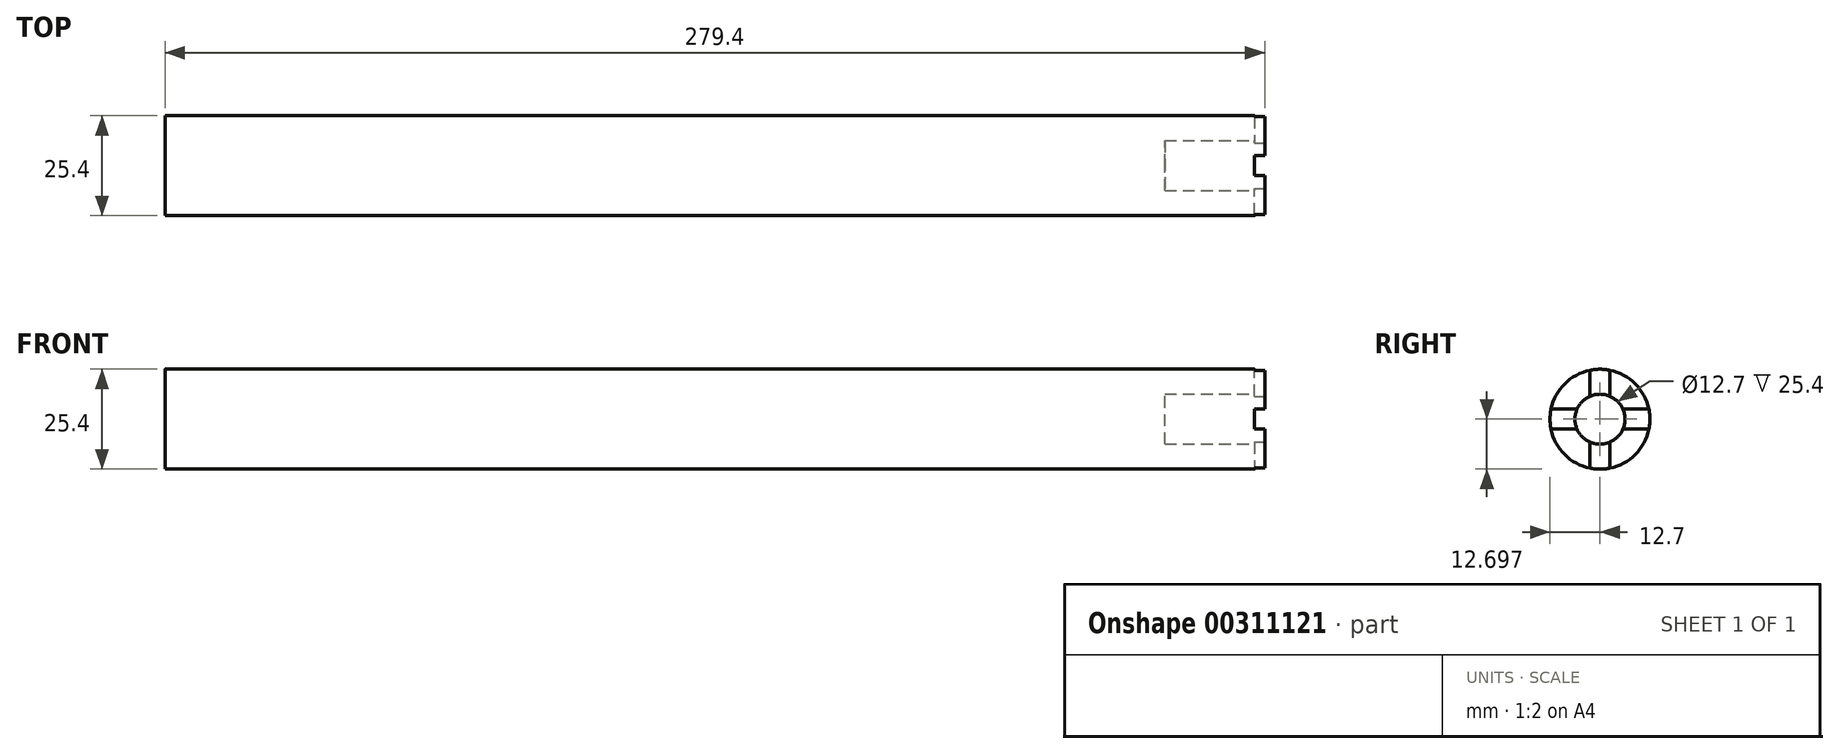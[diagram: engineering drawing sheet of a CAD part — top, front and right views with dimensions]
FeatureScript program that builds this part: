
annotation { "Feature Type Name" : "Feature", "Feature Type Description" : "" }
export const myFeature = defineFeature(function(context is Context, id is Id, definition is map)
    precondition{}
    {
        {
            var Q0;
            Q0=qCreatedBy(makeId("Right.planeOp"),FACE);
            var sketch = newSketch(context, id + "F0", { "sketchPlane" : qUnion([Q0])});
            skCircle(sketch, "E0", {"center": v(8.02, 19.48) * mm, "radius": 12.7 * mm});
            skSolve(sketch);
        }
        {
            var Q0;
            Q0 = qSketchRegion(id + "F0", true);
            extrude(context, id + "F1", {"entities" : qUnion([Q0]), "depth" : 279.4 * mm});
        }
        {
            var Q0;
            Q0=makeQuery(id+"F1.opExtrude","CAP_FACE",FACE,{"disambiguationData":[OSD([sQuery(id+"F0.wireOp",EDGE,"E0")])],"isStart":false});
            var sketch = newSketch(context, id + "F2", { "sketchPlane" : qUnion([Q0])});
            skLineSegment(sketch, "E1", {"start": v(10.56, 19.48) * mm, "end": v(10.56, 6.08) * mm});
            skLineSegment(sketch, "E2", {"start": v(10.56, 6.08) * mm, "end": v(5.48, 6.08) * mm});
            skLineSegment(sketch, "E3", {"start": v(5.48, 6.08) * mm, "end": v(5.48, 33) * mm});
            skLineSegment(sketch, "E4", {"start": v(5.48, 33) * mm, "end": v(10.56, 33) * mm});
            skLineSegment(sketch, "E5", {"start": v(10.56, 33) * mm, "end": v(10.56, 19.48) * mm});
            skLineSegment(sketch, "E6", {"start": v(8.02, 19.48) * mm, "end": v(8.02, 16.94) * mm});
            skLineSegment(sketch, "E7", {"start": v(8.02, 16.94) * mm, "end": v(21.67, 16.94) * mm});
            skLineSegment(sketch, "E8", {"start": v(21.67, 16.94) * mm, "end": v(21.67, 22.02) * mm});
            skLineSegment(sketch, "E9", {"start": v(21.67, 22.02) * mm, "end": v(-5.92, 22.02) * mm});
            skLineSegment(sketch, "E10", {"start": v(-5.92, 22.02) * mm, "end": v(-5.92, 16.94) * mm});
            skLineSegment(sketch, "E11", {"start": v(-5.92, 16.94) * mm, "end": v(8.02, 16.94) * mm});
            skSolve(sketch);
        }
        {
            var Q0;
            Q0=makeQuery(id+"F1.opExtrude","CAP_FACE",FACE,{"disambiguationData":[OSD([sQuery(id+"F0.wireOp",EDGE,"E0")])],"isStart":false});
            var sketch = newSketch(context, id + "F3", { "sketchPlane" : qUnion([Q0])});
            skCircle(sketch, "E12", {"center": v(8.02, 19.48) * mm, "radius": 6.35 * mm});
            skSolve(sketch);
        }
        {
            var Q0;
            Q0 = qSketchRegion(id + "F3", true);
            extrude(context, id + "F4", {"entities" : qUnion([Q0]), "operationType" : NewBodyOperationType.REMOVE, "oppositeDirection" : true, "depth" : 25.4 * mm});
        }
        {
            var Q0;
            Q0 = qSketchRegion(id + "F2", true);
            extrude(context, id + "F5", {"entities" : qUnion([Q0]), "operationType" : NewBodyOperationType.REMOVE, "oppositeDirection" : true, "depth" : 2.54 * mm});
        }
    });
